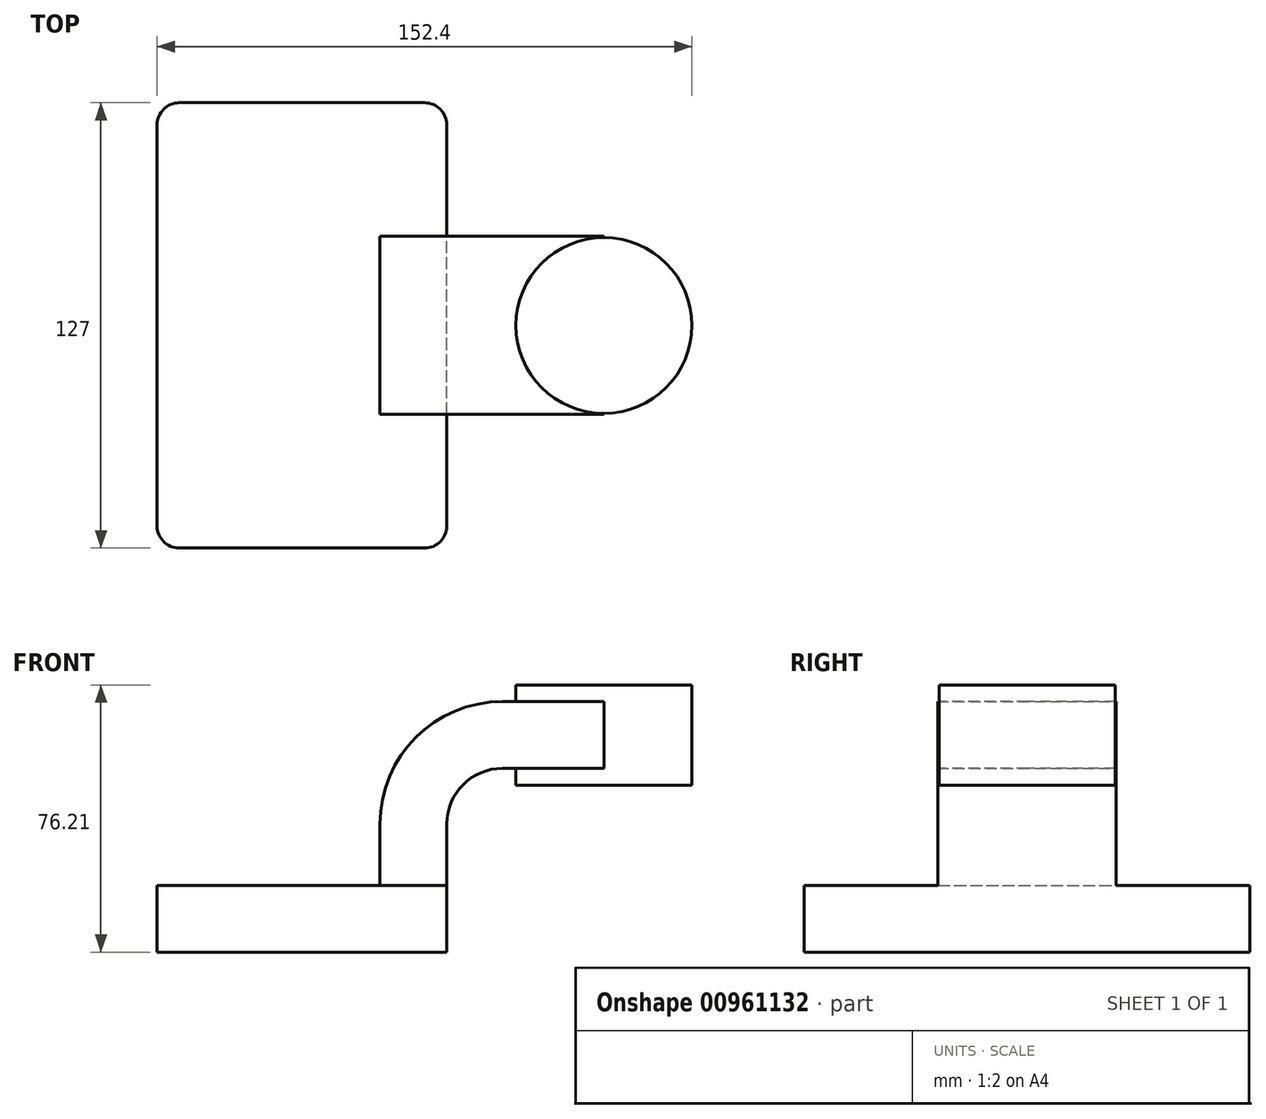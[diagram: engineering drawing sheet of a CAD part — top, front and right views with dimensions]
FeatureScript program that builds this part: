
annotation { "Feature Type Name" : "Feature", "Feature Type Description" : "" }
export const myFeature = defineFeature(function(context is Context, id is Id, definition is map)
    precondition{}
    {
        {
            var Q0;
            Q0=qCreatedBy(makeId("Front.planeOp"),FACE);
            var sketch = newSketch(context, id + "F0", { "sketchPlane" : qUnion([Q0])});
            skLineSegment(sketch, "E0.bottom", {"start": v(-41.28, -9.53) * mm, "end": v(41.28, -9.53) * mm});
            skLineSegment(sketch, "E0.top", {"start": v(-41.28, 9.53) * mm, "end": v(41.28, 9.53) * mm});
            skLineSegment(sketch, "E0.left", {"start": v(-41.28, -9.53) * mm, "end": v(-41.28, 9.53) * mm});
            skLineSegment(sketch, "E0.right", {"start": v(41.28, -9.53) * mm, "end": v(41.28, 9.52) * mm});
            skPoint(sketch, "E0.middle", {"position": v(0, 0) * mm});
            skLineSegment(sketch, "E1.bottom", {"start": v(60.32, 38.1) * mm, "end": v(111.12, 38.1) * mm});
            skLineSegment(sketch, "E1.top", {"start": v(60.32, 66.67) * mm, "end": v(111.12, 66.67) * mm});
            skLineSegment(sketch, "E1.left", {"start": v(60.32, 38.1) * mm, "end": v(60.32, 66.67) * mm});
            skLineSegment(sketch, "E1.right", {"start": v(111.12, 38.1) * mm, "end": v(111.12, 66.67) * mm});
            skPoint(sketch, "E1.middle", {"position": v(85.72, 52.39) * mm});
            skLineSegment(sketch, "E2", {"start": v(41.28, 9.52) * mm, "end": v(41.28, 27) * mm});
            skArc(sketch, "E3", {"start": v(41.27, 27) * mm, "mid": v(45.92, 38.23) * mm, "end": v(57.15, 42.88) * mm});
            skLineSegment(sketch, "E4", {"start": v(57.15, 42.88) * mm, "end": v(86.06, 42.88) * mm});
            skLineSegment(sketch, "E5.0", {"start": v(57.15, 61.93) * mm, "end": v(86.06, 61.93) * mm});
            skArc(sketch, "E5.1", {"start": v(22.22, 27) * mm, "mid": v(32.45, 51.7) * mm, "end": v(57.15, 61.93) * mm});
            skLineSegment(sketch, "E5.2", {"start": v(22.22, 9.52) * mm, "end": v(22.22, 27) * mm});
            skLineSegment(sketch, "E6", {"start": v(86.06, 38.1) * mm, "end": v(86.06, 66.67) * mm});
            skPoint(sketch, "E6.startSnap0", {"position": v(85.72, 38.1) * mm});
            skFitSpline(sketch, "E7", {"points": [v(-41.28, 9.53) * mm, v(57.15, 61.93) * mm], "startDerivative": vector(2.19, 101.12) * mm, "endDerivative": vector(78.86, 0) * mm});
            skSolve(sketch);
        }
        {
            var Q0;
            Q0=makeQuery(id+"F0.imprint","IMPRINT",FACE,{"disambiguationData":[TD([[makeQuery(id+"F0.imprint","IMPRINT",EDGE,{"derivedFrom":sQuery(id+"F0.wireOp",EDGE,"E0.bottom")}),1.0]])]});
            extrude(context, id + "F1", {"entities" : qUnion([Q0]), "endBound" : BoundingType.SYMMETRIC, "depth" : 127 * mm, "offsetDistance" : 25.4 * mm});
        }
        {
            var Q0;
            {var subQ1=sQuery(id+"F0.wireOp",EDGE,"E2");Q0=makeQuery(id+"F0.imprint","IMPRINT",FACE,{"disambiguationData":[TD([[makeQuery(id+"F0.imprint","IMPRINT",EDGE,{"derivedFrom":subQ1}),1.0]])]});}
            var Q1;
            {var subQ0=sQuery(id+"F0.wireOp",EDGE,"E4");var subQ1=sQuery(id+"F0.wireOp",EDGE,"E1.left");var subQ2=makeQuery(id+"F0.imprint","INTERSECT",VERTEX,{"derivedFrom":[subQ1,subQ0]});Q1=makeQuery(id+"F0.imprint","IMPRINT",FACE,{"disambiguationData":[TD([[makeQuery(id+"F0.imprint","IMPRINT",EDGE,{"disambiguationData":[TD([[subQ2,-1.0]])],"derivedFrom":subQ1}),-1.0]])]});}
            extrude(context, id + "F2", {"entities" : qUnion([Q0, Q1]), "operationType" : NewBodyOperationType.ADD, "endBound" : BoundingType.SYMMETRIC, "depth" : 50.8 * mm, "offsetDistance" : 25.4 * mm});
        }
        {
            var Q0;
            Q0=makeQuery(id+"F0.imprint","IMPRINT",FACE,{"disambiguationData":[TD([[makeQuery(id+"F0.imprint","IMPRINT",EDGE,{"derivedFrom":sQuery(id+"F0.wireOp",EDGE,"E5.1")}),1.0]])]});
            extrude(context, id + "F3", {"entities" : qUnion([Q0]), "operationType" : NewBodyOperationType.ADD, "endBound" : BoundingType.SYMMETRIC, "depth" : 15.88 * mm, "offsetDistance" : 25.4 * mm});
        }
        {
            var Q0;
            {var subQ0=sQuery(id+"F0.wireOp",EDGE,"E1.right");Q0=makeQuery(id+"F0.imprint","IMPRINT",FACE,{"disambiguationData":[TD([[makeQuery(id+"F0.imprint","IMPRINT",EDGE,{"derivedFrom":subQ0}),1.0]])]});}
            var Q1;
            Q1=sQuery(id+"F0.wireOp",EDGE,"E6");
            revolve(context, id + "F4", {"operationType" : NewBodyOperationType.ADD, "surfaceOperationType" : NewSurfaceOperationType.NEW, "entities" : qUnion([Q0]), "axis" : qUnion([Q1]), "revolveType" : RevolveType.FULL});
        }
        {
            var Q0;
            Q0=makeQuery(id+"F1.opExtrude","CAP_EDGE",EDGE,{"disambiguationData":[OSD([sQuery(id+"F0.wireOp",EDGE,"E0.left")])],"isStart":false});
            var Q1;
            Q1=makeQuery(id+"F1.opExtrude","CAP_EDGE",EDGE,{"disambiguationData":[OSD([sQuery(id+"F0.wireOp",EDGE,"E0.right")])],"isStart":false});
            var Q2;
            Q2=makeQuery(id+"F1.opExtrude","CAP_EDGE",EDGE,{"disambiguationData":[OSD([sQuery(id+"F0.wireOp",EDGE,"E0.right")])],"isStart":true});
            var Q3;
            Q3=makeQuery(id+"F1.opExtrude","CAP_EDGE",EDGE,{"disambiguationData":[OSD([sQuery(id+"F0.wireOp",EDGE,"E0.left")])],"isStart":true});
            fillet(context, id + "F5", {"entities" : qUnion([Q0, Q1, Q2, Q3]), "radius" : 6.35 * mm, "tangentPropagation" : true, "allowEdgeOverflow" : false});
        }
    });
